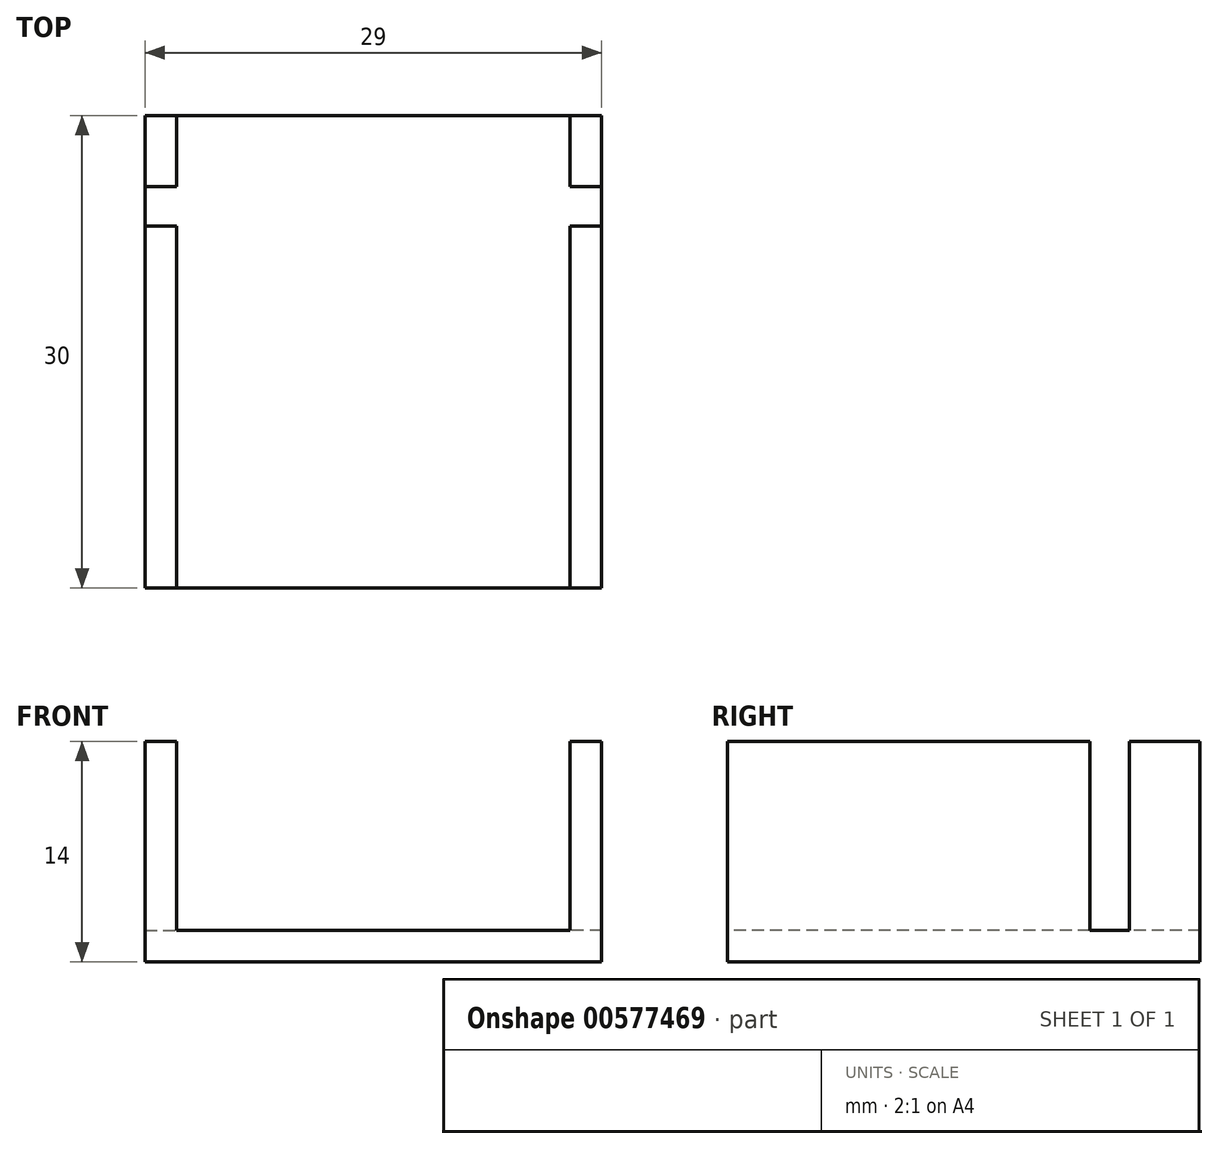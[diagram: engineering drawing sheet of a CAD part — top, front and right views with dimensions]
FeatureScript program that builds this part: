
annotation { "Feature Type Name" : "Feature", "Feature Type Description" : "" }
export const myFeature = defineFeature(function(context is Context, id is Id, definition is map)
    precondition{}
    {
        {
            var Q0;
            Q0=qCreatedBy(makeId("Top.planeOp"),FACE);
            var sketch = newSketch(context, id + "F0", { "sketchPlane" : qUnion([Q0])});
            skLineSegment(sketch, "E0.bottom", {"start": v(0, 0) * mm, "end": v(25, 0) * mm});
            skLineSegment(sketch, "E0.top", {"start": v(0, -30) * mm, "end": v(25, -30) * mm});
            skLineSegment(sketch, "E0.left", {"start": v(0, 0) * mm, "end": v(0, -30) * mm});
            skLineSegment(sketch, "E0.right", {"start": v(25, 0) * mm, "end": v(25, -30) * mm});
            skLineSegment(sketch, "E1.bottom", {"start": v(0, 0) * mm, "end": v(-2, 0) * mm});
            skLineSegment(sketch, "E1.top", {"start": v(0, -30) * mm, "end": v(-2, -30) * mm});
            skLineSegment(sketch, "E1.right", {"start": v(-2, 0) * mm, "end": v(-2, -30) * mm});
            skPoint(sketch, "E2", {"position": v(12.5, 0) * mm});
            skLineSegment(sketch, "E3", {"start": v(12.5, 0) * mm, "end": v(12.5, -30) * mm});
            skLineSegment(sketch, "E4.MirrorCS", {"start": v(27, 0) * mm, "end": v(27, -30) * mm});
            skLineSegment(sketch, "E5.MirrorCS", {"start": v(25, 0) * mm, "end": v(27, 0) * mm});
            skLineSegment(sketch, "E6.MirrorCS", {"start": v(25, -30) * mm, "end": v(27, -30) * mm});
            skLineSegment(sketch, "E7", {"start": v(-2, -7) * mm, "end": v(0, -7) * mm});
            skLineSegment(sketch, "E8.top", {"start": v(-2, -4.5) * mm, "end": v(0, -4.5) * mm});
            skLineSegment(sketch, "E8.left", {"start": v(-2, -7) * mm, "end": v(-2, -4.5) * mm});
            skLineSegment(sketch, "E8.right", {"start": v(0, -7) * mm, "end": v(0, -4.5) * mm});
            skLineSegment(sketch, "E9.MirrorCS", {"start": v(27, -4.5) * mm, "end": v(25, -4.5) * mm});
            skLineSegment(sketch, "E10.MirrorCS", {"start": v(27, -7) * mm, "end": v(25, -7) * mm});
            skSolve(sketch);
        }
        {
            var Q0;
            {var subQ6=sQuery(id+"F0.wireOp",EDGE,"E3");Q0=makeQuery(id+"F0.imprint","IMPRINT",FACE,{"disambiguationData":[TD([[makeQuery(id+"F0.imprint","IMPRINT",EDGE,{"derivedFrom":subQ6}),-1.0]])]});}
            var Q1;
            {var subQ7=sQuery(id+"F0.wireOp",EDGE,"E3");Q1=makeQuery(id+"F0.imprint","IMPRINT",FACE,{"disambiguationData":[TD([[makeQuery(id+"F0.imprint","IMPRINT",EDGE,{"derivedFrom":subQ7}),1.0]])]});}
            var Q2;
            Q2=makeQuery(id+"F0.imprint","IMPRINT",FACE,{"disambiguationData":[TD([[makeQuery(id+"F0.imprint","IMPRINT",EDGE,{"derivedFrom":sQuery(id+"F0.wireOp",EDGE,"E7")}),1.0]])]});
            var Q3;
            {var subQ0=sQuery(id+"F0.wireOp",EDGE,"E9.MirrorCS");Q3=makeQuery(id+"F0.imprint","IMPRINT",FACE,{"disambiguationData":[TD([[makeQuery(id+"F0.imprint","IMPRINT",EDGE,{"derivedFrom":subQ0}),1.0]])]});}
            extrude(context, id + "F1", {"entities" : qUnion([Q0, Q1, Q2, Q3]), "depth" : 2 * mm, "offsetDistance" : 25 * mm});
        }
        {
            var Q0;
            {var subQ0=sQuery(id+"F0.wireOp",EDGE,"E1.top");Q0=makeQuery(id+"F0.imprint","IMPRINT",FACE,{"disambiguationData":[TD([[makeQuery(id+"F0.imprint","IMPRINT",EDGE,{"derivedFrom":subQ0}),-1.0]])]});}
            var Q1;
            {var subQ0=sQuery(id+"F0.wireOp",EDGE,"E1.bottom");Q1=makeQuery(id+"F0.imprint","IMPRINT",FACE,{"disambiguationData":[TD([[makeQuery(id+"F0.imprint","IMPRINT",EDGE,{"derivedFrom":subQ0}),1.0]])]});}
            var Q2;
            {var subQ0=sQuery(id+"F0.wireOp",EDGE,"E5.MirrorCS");Q2=makeQuery(id+"F0.imprint","IMPRINT",FACE,{"disambiguationData":[TD([[makeQuery(id+"F0.imprint","IMPRINT",EDGE,{"derivedFrom":subQ0}),-1.0]])]});}
            var Q3;
            {var subQ0=sQuery(id+"F0.wireOp",EDGE,"E6.MirrorCS");Q3=makeQuery(id+"F0.imprint","IMPRINT",FACE,{"disambiguationData":[TD([[makeQuery(id+"F0.imprint","IMPRINT",EDGE,{"derivedFrom":subQ0}),1.0]])]});}
            extrude(context, id + "F2", {"entities" : qUnion([Q0, Q1, Q2, Q3]), "operationType" : NewBodyOperationType.ADD, "depth" : 14 * mm, "offsetDistance" : 25 * mm});
        }
    });
